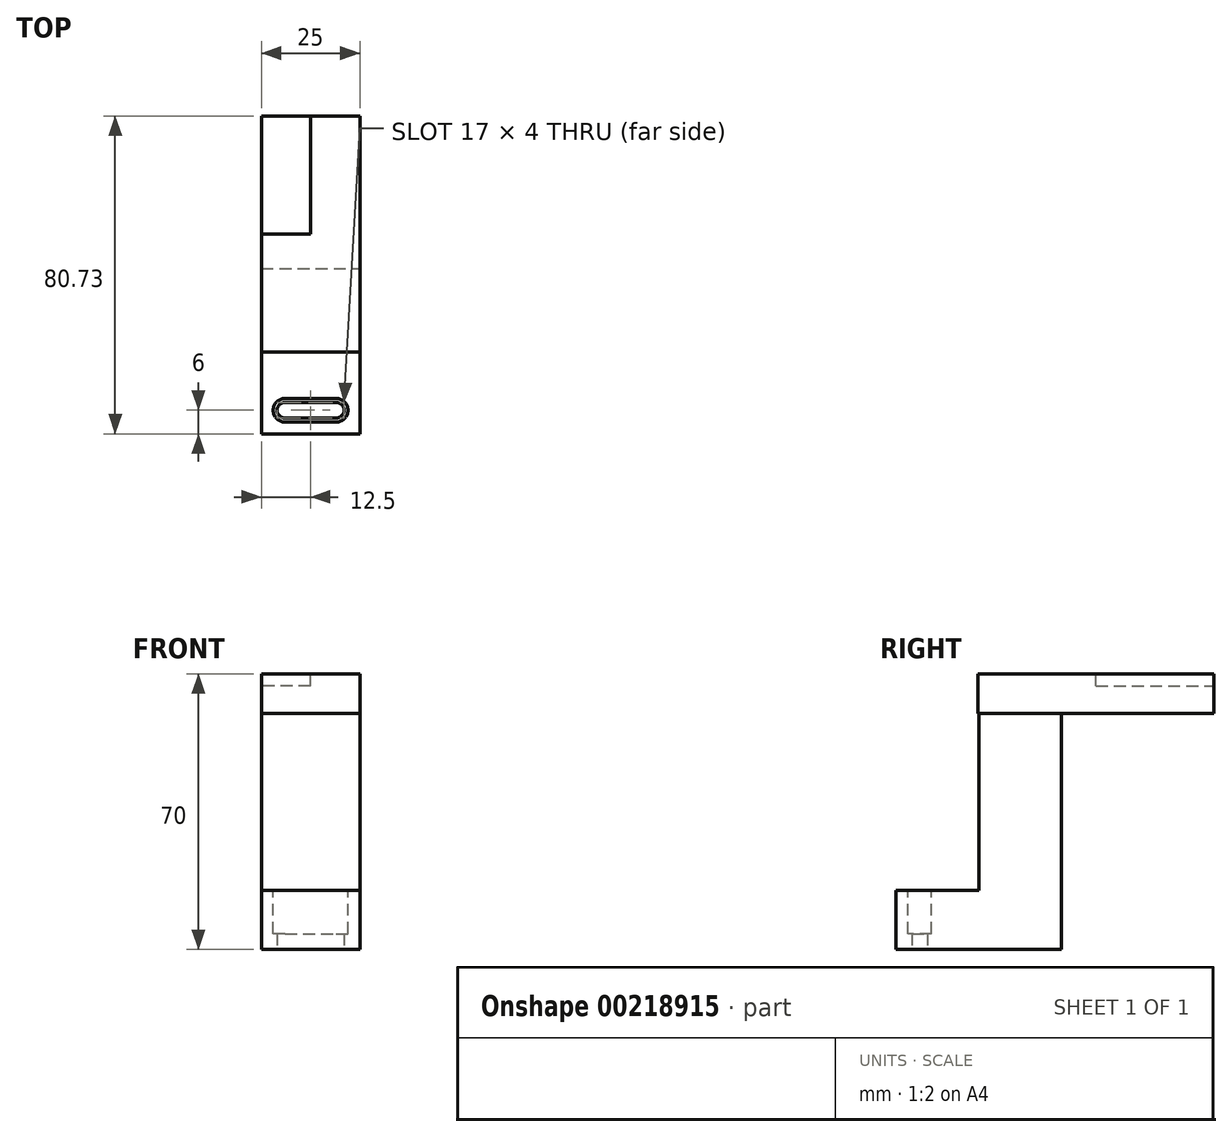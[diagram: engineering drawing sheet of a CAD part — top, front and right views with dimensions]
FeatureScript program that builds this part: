
annotation { "Feature Type Name" : "Feature", "Feature Type Description" : "" }
export const myFeature = defineFeature(function(context is Context, id is Id, definition is map)
    precondition{}
    {
        {
            var Q0;
            Q0=qCreatedBy(makeId("Top.planeOp"),FACE);
            var sketch = newSketch(context, id + "F0", { "sketchPlane" : qUnion([Q0])});
            skLineSegment(sketch, "E0.bottom", {"start": v(0, 0) * mm, "end": v(25, 0) * mm});
            skLineSegment(sketch, "E0.top", {"start": v(0, -42) * mm, "end": v(25, -42) * mm});
            skLineSegment(sketch, "E0.left", {"start": v(0, 0) * mm, "end": v(0, -42) * mm});
            skLineSegment(sketch, "E0.right", {"start": v(25, 0) * mm, "end": v(25, -42) * mm});
            skSolve(sketch);
        }
        {
            var Q0;
            Q0 = qSketchRegion(id + "F0", true);
            extrude(context, id + "F1", {"entities" : qUnion([Q0]), "depth" : 60 * mm, "offsetDistance" : 25 * mm});
        }
        {
            var Q0;
            Q0=makeQuery(id+"F1.opExtrude","CAP_FACE",FACE,{"disambiguationData":[OSD([sQuery(id+"F0.wireOp",EDGE,"E0.bottom"),sQuery(id+"F0.wireOp",EDGE,"E0.top"),sQuery(id+"F0.wireOp",EDGE,"E0.left"),sQuery(id+"F0.wireOp",EDGE,"E0.right")])],"isStart":false});
            var sketch = newSketch(context, id + "F2", { "sketchPlane" : qUnion([Q0])});
            skLineSegment(sketch, "E1.bottom", {"start": v(0, -21) * mm, "end": v(25, -21) * mm});
            skLineSegment(sketch, "E1.top", {"start": v(0, -42) * mm, "end": v(25, -42) * mm});
            skLineSegment(sketch, "E1.left", {"start": v(0, -21) * mm, "end": v(0, -42) * mm});
            skLineSegment(sketch, "E1.right", {"start": v(25, -21) * mm, "end": v(25, -42) * mm});
            skSolve(sketch);
        }
        {
            var Q0;
            Q0 = qSketchRegion(id + "F2", true);
            extrude(context, id + "F3", {"entities" : qUnion([Q0]), "operationType" : NewBodyOperationType.REMOVE, "oppositeDirection" : true, "depth" : 45 * mm, "offsetDistance" : 25 * mm});
        }
        {
            var Q0;
            Q0=makeQuery(id+"F1.opExtrude","CAP_FACE",FACE,{"disambiguationData":[OSD([sQuery(id+"F0.wireOp",EDGE,"E0.bottom"),sQuery(id+"F0.wireOp",EDGE,"E0.top"),sQuery(id+"F0.wireOp",EDGE,"E0.left"),sQuery(id+"F0.wireOp",EDGE,"E0.right")])],"isStart":true});
            var sketch = newSketch(context, id + "F4", { "sketchPlane" : qUnion([Q0])});
            skLineSegment(sketch, "E2", {"start": v(6, 38) * mm, "end": v(19, 38) * mm});
            skLineSegment(sketch, "E3", {"start": v(6, 34) * mm, "end": v(19, 34) * mm});
            skArc(sketch, "E4", {"start": v(19, 34) * mm, "mid": v(21, 36) * mm, "end": v(19, 38) * mm});
            skArc(sketch, "E5", {"start": v(6, 38) * mm, "mid": v(4, 36) * mm, "end": v(6, 34) * mm});
            skSolve(sketch);
        }
        {
            var Q0;
            Q0 = qSketchRegion(id + "F4", true);
            extrude(context, id + "F5", {"entities" : qUnion([Q0]), "operationType" : NewBodyOperationType.REMOVE, "oppositeDirection" : true, "depth" : 35 * mm, "offsetDistance" : 25 * mm});
        }
        {
            var Q0;
            Q0=makeQuery(id+"F3.boolean.opBoolean","COPY",FACE,{"derivedFrom":makeQuery(id+"F3.opExtrude","CAP_FACE",FACE,{"disambiguationData":[OSD([sQuery(id+"F2.wireOp",EDGE,"E1.bottom"),sQuery(id+"F2.wireOp",EDGE,"E1.top"),sQuery(id+"F2.wireOp",EDGE,"E1.left"),sQuery(id+"F2.wireOp",EDGE,"E1.right")])],"isStart":false})});
            var sketch = newSketch(context, id + "F6", { "sketchPlane" : qUnion([Q0])});
            skLineSegment(sketch, "E6", {"start": v(6, -39) * mm, "end": v(19, -39) * mm});
            skLineSegment(sketch, "E7", {"start": v(6, -33) * mm, "end": v(19, -33) * mm});
            skArc(sketch, "E8", {"start": v(6, -33) * mm, "mid": v(3, -36) * mm, "end": v(6, -39) * mm});
            skArc(sketch, "E9", {"start": v(19, -39) * mm, "mid": v(22, -36) * mm, "end": v(19, -33) * mm});
            skSolve(sketch);
        }
        {
            var Q0;
            Q0 = qSketchRegion(id + "F6", true);
            extrude(context, id + "F7", {"entities" : qUnion([Q0]), "operationType" : NewBodyOperationType.REMOVE, "oppositeDirection" : true, "depth" : 11 * mm, "offsetDistance" : 25 * mm});
        }
        {
            var Q0;
            Q0=qCreatedBy(makeId("Top.planeOp"),FACE);
            cPlane(context, id + "F8", {"entities" : qUnion([Q0]), "cplaneType" : CPlaneType.OFFSET, "offset" : 60 * mm, "width" : 150 * mm, "height" : 150 * mm});
        }
        {
            var Q0;
            Q0=qCreatedBy(id+"F8.planeOp",FACE);
            var sketch = newSketch(context, id + "F9", { "sketchPlane" : qUnion([Q0])});
            skLineSegment(sketch, "E10.bottom", {"start": v(25, -21.27) * mm, "end": v(0, -21.27) * mm});
            skLineSegment(sketch, "E10.top", {"start": v(25, 38.73) * mm, "end": v(0, 38.73) * mm});
            skLineSegment(sketch, "E10.left", {"start": v(25, -21.27) * mm, "end": v(25, 38.73) * mm});
            skLineSegment(sketch, "E10.right", {"start": v(0, -21.27) * mm, "end": v(0, 38.73) * mm});
            skSolve(sketch);
        }
        {
            var Q0;
            Q0=makeQuery(id+"F9.imprint","IMPRINT",FACE,{"disambiguationData":[TD([[makeQuery(id+"F9.imprint","IMPRINT",EDGE,{"derivedFrom":sQuery(id+"F9.wireOp",EDGE,"E10.bottom")}),-1.0]])]});
            extrude(context, id + "F10", {"entities" : qUnion([Q0]), "depth" : 10 * mm, "offsetDistance" : 25 * mm});
        }
        {
            var Q0;
            Q0=makeQuery(id+"F10.opExtrude","CAP_FACE",FACE,{"disambiguationData":[OSD([sQuery(id+"F9.wireOp",EDGE,"E10.bottom"),sQuery(id+"F9.wireOp",EDGE,"E10.top"),sQuery(id+"F9.wireOp",EDGE,"E10.left"),sQuery(id+"F9.wireOp",EDGE,"E10.right")])],"isStart":false});
            var sketch = newSketch(context, id + "F11", { "sketchPlane" : qUnion([Q0])});
            skLineSegment(sketch, "E11.bottom", {"start": v(0, 8.73) * mm, "end": v(12.5, 8.73) * mm});
            skLineSegment(sketch, "E11.top", {"start": v(0, 38.73) * mm, "end": v(12.5, 38.73) * mm});
            skLineSegment(sketch, "E11.left", {"start": v(0, 8.73) * mm, "end": v(0, 38.73) * mm});
            skLineSegment(sketch, "E11.right", {"start": v(12.5, 8.73) * mm, "end": v(12.5, 38.73) * mm});
            skSolve(sketch);
        }
        {
            var Q0;
            Q0 = qSketchRegion(id + "F11", true);
            extrude(context, id + "F12", {"entities" : qUnion([Q0]), "operationType" : NewBodyOperationType.REMOVE, "oppositeDirection" : true, "depth" : 3 * mm, "offsetDistance" : 25 * mm});
        }
    });
